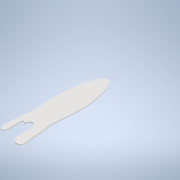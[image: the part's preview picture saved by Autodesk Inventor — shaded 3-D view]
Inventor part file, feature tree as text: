
AUTODESK INVENTOR PART (.ipt)
format: ipt  version: 2021 (Build 250183000, 183)  size: 178,688 bytes
history: native  units: in
note: dims shown in document units (in); Inventor stores cm internally (conversion verified against a paired STEP export)
features: fillet x3, extrude x1, sketch x1
ambient origin geometry x8: Origin, YZ Plane, XZ Plane, XY Plane, X Axis, Y Axis, Z Axis, Center Point
bodies: Body1 (feature_tree)
feature tree (5):
  extrude  "Extrusion2"  Depth=0.25in
  fillet  "Fillet2"  Radius=1.5in
  fillet  "Fillet3"  Radius=2.0in
  fillet  "Fillet4"  Radius=8.5in
  sketch  "Sketch2"  dims[d19=5.5in d20=9.25in d24=1.5in d35=2.0in d37=8.5in d51=0.25in d52=2.0in d60=180.0deg d61=4.5in d76=180.0deg d81=0.25in d82=90.0deg d83=0.125in d84=2.0in d85=2.75in d86=1.5in d98=2.5in d99=180.0deg d100=1.25in d101=90.0deg d102=3.0in d106=9.75in d107=4.875in d108=9.0in d109=0.375in d110=0.0in d111=0.25in d112=0.25in d113=0.25in]
